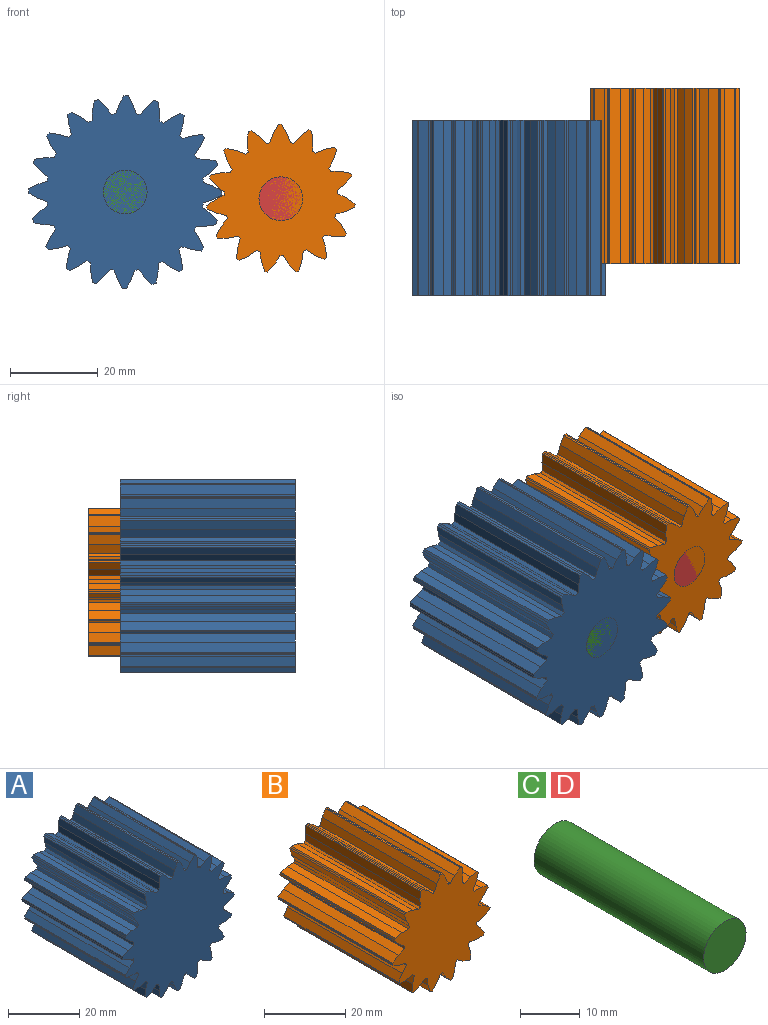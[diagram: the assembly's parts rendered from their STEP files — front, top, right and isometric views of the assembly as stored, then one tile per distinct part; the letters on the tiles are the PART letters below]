
ASSEMBLY  parts=4 mates=2
PART A: 142 faces, bbox 44x40x44 mm
  f0: plane 40x2.14mm, normal (-0.96,0,-0.28), area 89mm2, adj f1,f139,f140,f141
  f1: cylinder r=18mm len=40mm, axis (0,1,0), area 39.3mm2, adj f0,f2,f140,f141
  f2: plane 40x2.14mm, normal (0.28,0,0.96), area 89mm2, adj f1,f3,f140,f141
  f3: plane 40x2.29mm, normal (0.15,0,0.99), area 92.7mm2, adj f2,f4,f140,f141
  f4: plane 40x0.4mm, normal (-0.8,0,0.6), area 20mm2, adj f3,f5,f140,f141
  f5: plane 40x0.41mm, normal (-0.82,0,0.58), area 20mm2, adj f4,f6,f140,f141
  f6: plane 40x2.07mm, normal (-0.89,0,-0.45), area 92.7mm2, adj f5,f7,f140,f141
  f7: plane 40x1.84mm, normal (-0.83,0,-0.56), area 89mm2, adj f6,f8,f140,f141
  f8: cylinder r=18mm len=40mm, axis (0,1,0), area 39.3mm2, adj f7,f9,f140,f141
  f9: plane 40x2.22mm, normal (-0.03,0,1), area 89mm2, adj f8,f10,f140,f141
  f10: plane 40x2.29mm, normal (-0.16,0,0.99), area 92.7mm2, adj f9,f11,f140,f141
  f11: plane 40x0.47mm, normal (-0.95,0,0.32), area 20mm2, adj f10,f12,f140,f141
  f12: plane 40x0.48mm, normal (-0.95,0,0.3), area 20mm2, adj f11,f13,f140,f141
  f13: plane 40x1.65mm, normal (-0.71,0,-0.7), area 92.7mm2, adj f12,f14,f140,f141
  f14: plane 40x1.75mm, normal (-0.62,0,-0.79), area 89mm2, adj f13,f15,f140,f141
  f15: cylinder r=18mm len=40mm, axis (0,1,0), area 39.3mm2, adj f14,f16,f140,f141
  f16: plane 40x2.09mm, normal (-0.34,0,0.94), area 89mm2, adj f15,f17,f140,f141
  f17: plane 40x2.06mm, normal (-0.46,0,0.89), area 92.7mm2, adj f16,f18,f140,f141
  f18: plane 40x0.5mm, normal (-1,0,0.01), area 20mm2, adj f17,f19,f140,f141
  f19: plane 40x0.5mm, normal (-1,0,-0.01), area 20mm2, adj f18,f20,f140,f141
  f20: plane 40x2.06mm, normal (-0.46,0,-0.89), area 92.7mm2, adj f19,f21,f140,f141
  f21: plane 40x2.09mm, normal (-0.34,0,-0.94), area 89mm2, adj f20,f22,f140,f141
  f22: cylinder r=18mm len=40mm, axis (0,1,0), area 39.3mm2, adj f21,f23,f140,f141
  f23: plane 40x1.75mm, normal (-0.62,0,0.79), area 89mm2, adj f22,f24,f140,f141
  f24: plane 40x1.65mm, normal (-0.71,0,0.7), area 92.7mm2, adj f23,f25,f140,f141
  f25: plane 40x0.48mm, normal (-0.95,0,-0.3), area 20mm2, adj f24,f26,f140,f141
  f26: plane 40x0.47mm, normal (-0.95,0,-0.32), area 20mm2, adj f25,f27,f140,f141
  f27: plane 40x2.29mm, normal (-0.16,0,-0.99), area 92.7mm2, adj f26,f28,f140,f141
  f28: plane 40x2.22mm, normal (-0.03,0,-1), area 89mm2, adj f27,f29,f140,f141
  f29: cylinder r=18mm len=40mm, axis (0,1,0), area 39.3mm2, adj f28,f30,f140,f141
  f30: plane 40x1.84mm, normal (-0.83,0,0.56), area 89mm2, adj f29,f31,f140,f141
  f31: plane 40x2.07mm, normal (-0.89,0,0.45), area 92.7mm2, adj f30,f32,f140,f141
  f32: plane 40x0.41mm, normal (-0.82,0,-0.58), area 20mm2, adj f31,f33,f140,f141
  f33: plane 40x0.4mm, normal (-0.8,0,-0.6), area 20mm2, adj f32,f34,f140,f141
  f34: plane 40x2.29mm, normal (0.15,0,-0.99), area 92.7mm2, adj f33,f35,f140,f141
  f35: plane 40x2.14mm, normal (0.28,0,-0.96), area 89mm2, adj f34,f36,f140,f141
  f36: cylinder r=18mm len=40mm, axis (0,1,0), area 39.3mm2, adj f35,f37,f140,f141
  f37: plane 40x2.14mm, normal (-0.96,0,0.28), area 89mm2, adj f36,f38,f140,f141
  f38: plane 40x2.29mm, normal (-0.99,0,0.15), area 92.7mm2, adj f37,f39,f140,f141
  f39: plane 40x0.4mm, normal (-0.6,0,-0.8), area 20mm2, adj f38,f40,f140,f141
  f40: plane 40x0.41mm, normal (-0.58,0,-0.82), area 20mm2, adj f39,f41,f140,f141
  f41: plane 40x2.07mm, normal (0.45,0,-0.89), area 92.7mm2, adj f40,f42,f140,f141
  f42: plane 40x1.84mm, normal (0.56,0,-0.83), area 89mm2, adj f41,f43,f140,f141
  f43: cylinder r=18mm len=40mm, axis (0,1,0), area 39.3mm2, adj f42,f44,f140,f141
  f44: plane 40x2.22mm, normal (-1,0,-0.03), area 89mm2, adj f43,f45,f140,f141
  f45: plane 40x2.29mm, normal (-0.99,0,-0.16), area 92.7mm2, adj f44,f46,f140,f141
  f46: plane 40x0.47mm, normal (-0.32,0,-0.95), area 20mm2, adj f45,f47,f140,f141
  f47: plane 40x0.48mm, normal (-0.3,0,-0.95), area 20mm2, adj f46,f48,f140,f141
  f48: plane 40x1.65mm, normal (0.7,0,-0.71), area 92.7mm2, adj f47,f49,f140,f141
  f49: plane 40x1.75mm, normal (0.79,0,-0.62), area 89mm2, adj f48,f50,f140,f141
  f50: cylinder r=18mm len=40mm, axis (0,1,0), area 39.3mm2, adj f49,f51,f140,f141
  f51: plane 40x2.09mm, normal (-0.94,0,-0.34), area 89mm2, adj f50,f52,f140,f141
  f52: plane 40x2.06mm, normal (-0.89,0,-0.46), area 92.7mm2, adj f51,f53,f140,f141
  f53: plane 40x0.5mm, normal (-0.01,0,-1), area 20mm2, adj f52,f54,f140,f141
  f54: plane 40x0.5mm, normal (0.01,0,-1), area 20mm2, adj f53,f55,f140,f141
  f55: plane 40x2.06mm, normal (0.89,0,-0.46), area 92.7mm2, adj f54,f56,f140,f141
  f56: plane 40x2.09mm, normal (0.94,0,-0.34), area 89mm2, adj f55,f57,f140,f141
  f57: cylinder r=18mm len=40mm, axis (0,1,0), area 39.3mm2, adj f56,f58,f140,f141
  f58: plane 40x1.75mm, normal (-0.79,0,-0.62), area 89mm2, adj f57,f59,f140,f141
  f59: plane 40x1.65mm, normal (-0.7,0,-0.71), area 92.7mm2, adj f58,f60,f140,f141
  f60: plane 40x0.48mm, normal (0.3,0,-0.95), area 20mm2, adj f59,f61,f140,f141
  f61: plane 40x0.47mm, normal (0.32,0,-0.95), area 20mm2, adj f60,f62,f140,f141
  f62: plane 40x2.29mm, normal (0.99,0,-0.16), area 92.7mm2, adj f61,f63,f140,f141
  f63: plane 40x2.22mm, normal (1,0,-0.03), area 89mm2, adj f62,f64,f140,f141
  f64: cylinder r=18mm len=40mm, axis (0,1,0), area 39.3mm2, adj f63,f65,f140,f141
  f65: plane 40x1.84mm, normal (-0.56,0,-0.83), area 89mm2, adj f64,f66,f140,f141
  f66: plane 40x2.07mm, normal (-0.45,0,-0.89), area 92.7mm2, adj f65,f67,f140,f141
  f67: plane 40x0.41mm, normal (0.58,0,-0.82), area 20mm2, adj f66,f68,f140,f141
  f68: plane 40x0.4mm, normal (0.6,0,-0.8), area 20mm2, adj f67,f69,f140,f141
  f69: plane 40x2.29mm, normal (0.99,0,0.15), area 92.7mm2, adj f68,f70,f140,f141
  f70: plane 40x2.14mm, normal (0.96,0,0.28), area 89mm2, adj f69,f71,f140,f141
  f71: cylinder r=18mm len=40mm, axis (0,1,0), area 39.3mm2, adj f70,f72,f140,f141
  f72: plane 40x2.14mm, normal (-0.28,0,-0.96), area 89mm2, adj f71,f73,f140,f141
  f73: plane 40x2.29mm, normal (-0.15,0,-0.99), area 92.7mm2, adj f72,f74,f140,f141
  f74: plane 40x0.4mm, normal (0.8,0,-0.6), area 20mm2, adj f73,f75,f140,f141
  f75: plane 40x0.41mm, normal (0.82,0,-0.58), area 20mm2, adj f74,f76,f140,f141
  f76: plane 40x2.07mm, normal (0.89,0,0.45), area 92.7mm2, adj f75,f77,f140,f141
  f77: plane 40x1.84mm, normal (0.83,0,0.56), area 89mm2, adj f76,f78,f140,f141
  f78: cylinder r=18mm len=40mm, axis (0,1,0), area 39.3mm2, adj f77,f79,f140,f141
  f79: plane 40x2.22mm, normal (0.03,0,-1), area 89mm2, adj f78,f80,f140,f141
  f80: plane 40x2.29mm, normal (0.16,0,-0.99), area 92.7mm2, adj f79,f81,f140,f141
  f81: plane 40x0.47mm, normal (0.95,0,-0.32), area 20mm2, adj f80,f82,f140,f141
  f82: plane 40x0.48mm, normal (0.95,0,-0.3), area 20mm2, adj f81,f83,f140,f141
  f83: plane 40x1.65mm, normal (0.71,0,0.7), area 92.7mm2, adj f82,f84,f140,f141
  f84: plane 40x1.75mm, normal (0.62,0,0.79), area 89mm2, adj f83,f85,f140,f141
  f85: cylinder r=18mm len=40mm, axis (0,1,0), area 39.3mm2, adj f84,f86,f140,f141
  f86: plane 40x2.09mm, normal (0.34,0,-0.94), area 89mm2, adj f85,f87,f140,f141
  f87: plane 40x2.06mm, normal (0.46,0,-0.89), area 92.7mm2, adj f86,f88,f140,f141
  f88: plane 40x0.5mm, normal (1,0,-0.01), area 20mm2, adj f87,f89,f140,f141
  f89: plane 40x0.5mm, normal (1,0,0.01), area 20mm2, adj f88,f90,f140,f141
  f90: plane 40x2.06mm, normal (0.46,0,0.89), area 92.7mm2, adj f89,f91,f140,f141
  f91: plane 40x2.09mm, normal (0.34,0,0.94), area 89mm2, adj f90,f92,f140,f141
  f92: cylinder r=18mm len=40mm, axis (0,1,0), area 39.3mm2, adj f91,f93,f140,f141
  f93: plane 40x1.75mm, normal (0.62,0,-0.79), area 89mm2, adj f92,f94,f140,f141
  f94: plane 40x1.65mm, normal (0.71,0,-0.7), area 92.7mm2, adj f93,f95,f140,f141
  f95: plane 40x0.48mm, normal (0.95,0,0.3), area 20mm2, adj f94,f96,f140,f141
  f96: plane 40x0.47mm, normal (0.95,0,0.32), area 20mm2, adj f95,f97,f140,f141
  f97: plane 40x2.29mm, normal (0.16,0,0.99), area 92.7mm2, adj f96,f98,f140,f141
  f98: plane 40x2.22mm, normal (0.03,0,1), area 89mm2, adj f97,f99,f140,f141
  f99: cylinder r=18mm len=40mm, axis (0,1,0), area 39.3mm2, adj f98,f100,f140,f141
  f100: plane 40x1.84mm, normal (0.83,0,-0.56), area 89mm2, adj f99,f101,f140,f141
  f101: plane 40x2.07mm, normal (0.89,0,-0.45), area 92.7mm2, adj f100,f102,f140,f141
  f102: plane 40x0.41mm, normal (0.82,0,0.58), area 20mm2, adj f101,f103,f140,f141
  f103: plane 40x0.4mm, normal (0.8,0,0.6), area 20mm2, adj f102,f104,f140,f141
  f104: plane 40x2.29mm, normal (-0.15,0,0.99), area 92.7mm2, adj f103,f105,f140,f141
  f105: plane 40x2.14mm, normal (-0.28,0,0.96), area 89mm2, adj f104,f106,f140,f141
  f106: cylinder r=18mm len=40mm, axis (0,1,0), area 39.3mm2, adj f105,f107,f140,f141
  f107: plane 40x2.14mm, normal (0.96,0,-0.28), area 89mm2, adj f106,f108,f140,f141
  f108: plane 40x2.29mm, normal (0.99,0,-0.15), area 92.7mm2, adj f107,f109,f140,f141
  f109: plane 40x0.4mm, normal (0.6,0,0.8), area 20mm2, adj f108,f110,f140,f141
  f110: plane 40x0.41mm, normal (0.58,0,0.82), area 20mm2, adj f109,f111,f140,f141
  f111: plane 40x2.07mm, normal (-0.45,0,0.89), area 92.7mm2, adj f110,f112,f140,f141
  f112: plane 40x1.84mm, normal (-0.56,0,0.83), area 89mm2, adj f111,f113,f140,f141
  f113: cylinder r=18mm len=40mm, axis (0,1,0), area 39.3mm2, adj f112,f114,f140,f141
  f114: plane 40x2.22mm, normal (1,0,0.03), area 89mm2, adj f113,f115,f140,f141
  f115: plane 40x2.29mm, normal (0.99,0,0.16), area 92.7mm2, adj f114,f116,f140,f141
  f116: plane 40x0.47mm, normal (0.32,0,0.95), area 20mm2, adj f115,f117,f140,f141
  f117: plane 40x0.48mm, normal (0.3,0,0.95), area 20mm2, adj f116,f118,f140,f141
  f118: plane 40x1.65mm, normal (-0.7,0,0.71), area 92.7mm2, adj f117,f119,f140,f141
  f119: plane 40x1.75mm, normal (-0.79,0,0.62), area 89mm2, adj f118,f120,f140,f141
  f120: cylinder r=18mm len=40mm, axis (0,1,0), area 39.3mm2, adj f119,f121,f140,f141
  f121: plane 40x2.09mm, normal (0.94,0,0.34), area 89mm2, adj f120,f122,f140,f141
  f122: plane 40x2.06mm, normal (0.89,0,0.46), area 92.7mm2, adj f121,f123,f140,f141
  f123: plane 40x0.5mm, normal (0.01,0,1), area 20mm2, adj f122,f124,f140,f141
  f124: plane 40x0.5mm, normal (-0.01,0,1), area 20mm2, adj f123,f125,f140,f141
  f125: plane 40x2.06mm, normal (-0.89,0,0.46), area 92.7mm2, adj f124,f126,f140,f141
  f126: plane 40x2.09mm, normal (-0.94,0,0.34), area 89mm2, adj f125,f127,f140,f141
  f127: cylinder r=18mm len=40mm, axis (0,1,0), area 39.3mm2, adj f126,f128,f140,f141
  f128: plane 40x1.75mm, normal (0.79,0,0.62), area 89mm2, adj f127,f129,f140,f141
  f129: plane 40x1.65mm, normal (0.7,0,0.71), area 92.7mm2, adj f128,f130,f140,f141
  f130: plane 40x0.48mm, normal (-0.3,0,0.95), area 20mm2, adj f129,f131,f140,f141
  f131: plane 40x0.47mm, normal (-0.32,0,0.95), area 20mm2, adj f130,f132,f140,f141
  f132: plane 40x2.29mm, normal (-0.99,0,0.16), area 92.7mm2, adj f131,f133,f140,f141
  f133: plane 40x2.22mm, normal (-1,0,0.03), area 89mm2, adj f132,f134,f140,f141
  f134: cylinder r=18mm len=40mm, axis (0,1,0), area 39.3mm2, adj f133,f135,f140,f141
  f135: plane 40x1.84mm, normal (0.56,0,0.83), area 89mm2, adj f134,f136,f140,f141
  f136: plane 40x2.07mm, normal (0.45,0,0.89), area 92.7mm2, adj f135,f137,f140,f141
  f137: plane 40x0.41mm, normal (-0.58,0,0.82), area 20mm2, adj f136,f138,f140,f141
  f138: plane 40x0.4mm, normal (-0.6,0,0.8), area 20mm2, adj f137,f139,f140,f141
  f139: plane 40x2.29mm, normal (-0.99,0,-0.15), area 92.7mm2, adj f0,f138,f140,f141
  f140: plane 44x44mm, normal (0,-1,0), area 1256.5mm2, adj f0,f1,f2,f3,f4,f5,f6,f7
  f141: plane 44x44mm, normal (0,1,0), area 1256.5mm2, adj f0,f1,f2,f3,f4,f5,f6,f7
PART B: 107 faces, bbox 33.9x40x33.7 mm
  f0: cylinder r=13mm len=40mm, axis (0,1,0), area 29.3mm2, adj f1,f104,f105,f106
  f1: plane 40x2.1mm, normal (0.37,0,0.93), area 90.7mm2, adj f0,f2,f105,f106
  f2: plane 40x2.35mm, normal (0.21,0,0.98), area 96mm2, adj f1,f3,f105,f106
  f3: plane 40x0.27mm, normal (-0.74,0,0.68), area 14.7mm2, adj f2,f4,f105,f106
  f4: plane 40x0.28mm, normal (-0.75,0,0.66), area 14.7mm2, adj f3,f5,f105,f106
  f5: plane 40x2.28mm, normal (-0.95,0,-0.31), area 96mm2, adj f4,f6,f105,f106
  f6: plane 40x2mm, normal (-0.88,0,-0.47), area 90.7mm2, adj f5,f7,f105,f106
  f7: cylinder r=13mm len=40mm, axis (0,1,0), area 29.3mm2, adj f6,f8,f105,f106
  f8: plane 40x2.27mm, normal (-0.03,0,1), area 90.7mm2, adj f7,f9,f105,f106
  f9: plane 40x2.35mm, normal (-0.21,0,0.98), area 96mm2, adj f8,f10,f105,f106
  f10: plane 40x0.35mm, normal (-0.95,0,0.32), area 14.7mm2, adj f9,f11,f105,f106
  f11: plane 40x0.35mm, normal (-0.95,0,0.3), area 14.7mm2, adj f10,f12,f105,f106
  f12: plane 40x1.78mm, normal (-0.74,0,-0.67), area 96mm2, adj f11,f13,f105,f106
  f13: plane 40x1.79mm, normal (-0.62,0,-0.79), area 90.7mm2, adj f12,f14,f105,f106
  f14: cylinder r=13mm len=40mm, axis (0,1,0), area 29.3mm2, adj f13,f15,f105,f106
  f15: plane 40x2.04mm, normal (-0.44,0,0.9), area 90.7mm2, adj f14,f16,f105,f106
  f16: plane 40x1.94mm, normal (-0.59,0,0.81), area 96mm2, adj f15,f17,f105,f106
  f17: plane 40x0.37mm, normal (-1,0,-0.09), area 14.7mm2, adj f16,f18,f105,f106
  f18: plane 40x0.36mm, normal (-0.99,0,-0.12), area 14.7mm2, adj f17,f19,f105,f106
  f19: plane 40x2.19mm, normal (-0.41,0,-0.91), area 96mm2, adj f18,f20,f105,f106
  f20: plane 40x2.2mm, normal (-0.24,0,-0.97), area 90.7mm2, adj f19,f21,f105,f106
  f21: cylinder r=13mm len=40mm, axis (0,1,0), area 29.3mm2, adj f20,f22,f105,f106
  f22: plane 40x1.74mm, normal (-0.77,0,0.64), area 90.7mm2, adj f21,f23,f105,f106
  f23: plane 40x2.08mm, normal (-0.87,0,0.5), area 96mm2, adj f22,f24,f105,f106
  f24: plane 40x0.32mm, normal (-0.87,0,-0.49), area 14.7mm2, adj f23,f25,f105,f106
  f25: plane 40x0.32mm, normal (-0.86,0,-0.51), area 14.7mm2, adj f24,f26,f105,f106
  f26: plane 40x2.4mm, normal (0,0,-1), area 96mm2, adj f25,f27,f105,f106
  f27: plane 40x2.23mm, normal (0.17,0,-0.98), area 90.7mm2, adj f26,f28,f105,f106
  f28: cylinder r=13mm len=40mm, axis (0,1,0), area 29.3mm2, adj f27,f29,f105,f106
  f29: plane 40x2.18mm, normal (-0.96,0,0.28), area 90.7mm2, adj f28,f30,f105,f106
  f30: plane 40x2.39mm, normal (-0.99,0,0.1), area 96mm2, adj f29,f31,f105,f106
  f31: plane 40x0.29mm, normal (-0.6,0,-0.8), area 14.7mm2, adj f30,f32,f105,f106
  f32: plane 40x0.3mm, normal (-0.58,0,-0.82), area 14.7mm2, adj f31,f33,f105,f106
  f33: plane 40x2.19mm, normal (0.41,0,-0.91), area 96mm2, adj f32,f34,f105,f106
  f34: plane 40x1.88mm, normal (0.56,0,-0.83), area 90.7mm2, adj f33,f35,f105,f106
  f35: cylinder r=13mm len=40mm, axis (0,1,0), area 29.3mm2, adj f34,f36,f105,f106
  f36: plane 40x2.25mm, normal (-0.99,0,-0.14), area 90.7mm2, adj f35,f37,f105,f106
  f37: plane 40x2.28mm, normal (-0.95,0,-0.31), area 96mm2, adj f36,f38,f105,f106
  f38: plane 40x0.36mm, normal (-0.22,0,-0.98), area 14.7mm2, adj f37,f39,f105,f106
  f39: plane 40x0.36mm, normal (-0.2,0,-0.98), area 14.7mm2, adj f38,f40,f105,f106
  f40: plane 40x1.78mm, normal (0.74,0,-0.67), area 96mm2, adj f39,f41,f105,f106
  f41: plane 40x1.92mm, normal (0.85,0,-0.53), area 90.7mm2, adj f40,f42,f105,f106
  f42: cylinder r=13mm len=40mm, axis (0,1,0), area 29.3mm2, adj f41,f43,f105,f106
  f43: plane 40x1.92mm, normal (-0.85,0,-0.53), area 90.7mm2, adj f42,f44,f105,f106
  f44: plane 40x1.78mm, normal (-0.74,0,-0.67), area 96mm2, adj f43,f45,f105,f106
  f45: plane 40x0.36mm, normal (0.2,0,-0.98), area 14.7mm2, adj f44,f46,f105,f106
  f46: plane 40x0.36mm, normal (0.22,0,-0.98), area 14.7mm2, adj f45,f47,f105,f106
  f47: plane 40x2.28mm, normal (0.95,0,-0.31), area 96mm2, adj f46,f48,f105,f106
  f48: plane 40x2.25mm, normal (0.99,0,-0.14), area 90.7mm2, adj f47,f49,f105,f106
  f49: cylinder r=13mm len=40mm, axis (0,1,0), area 29.3mm2, adj f48,f50,f105,f106
  f50: plane 40x1.88mm, normal (-0.56,0,-0.83), area 90.7mm2, adj f49,f51,f105,f106
  f51: plane 40x2.19mm, normal (-0.41,0,-0.91), area 96mm2, adj f50,f52,f105,f106
  f52: plane 40x0.3mm, normal (0.58,0,-0.82), area 14.7mm2, adj f51,f53,f105,f106
  f53: plane 40x0.29mm, normal (0.6,0,-0.8), area 14.7mm2, adj f52,f54,f105,f106
  f54: plane 40x2.39mm, normal (0.99,0,0.1), area 96mm2, adj f53,f55,f105,f106
  f55: plane 40x2.18mm, normal (0.96,0,0.28), area 90.7mm2, adj f54,f56,f105,f106
  f56: cylinder r=13mm len=40mm, axis (0,1,0), area 29.3mm2, adj f55,f57,f105,f106
  f57: plane 40x2.23mm, normal (-0.17,0,-0.98), area 90.7mm2, adj f56,f58,f105,f106
  f58: plane 40x2.4mm, normal (0,0,-1), area 96mm2, adj f57,f59,f105,f106
  f59: plane 40x0.32mm, normal (0.86,0,-0.51), area 14.7mm2, adj f58,f60,f105,f106
  f60: plane 40x0.32mm, normal (0.87,0,-0.49), area 14.7mm2, adj f59,f61,f105,f106
  f61: plane 40x2.08mm, normal (0.87,0,0.5), area 96mm2, adj f60,f62,f105,f106
  f62: plane 40x1.74mm, normal (0.77,0,0.64), area 90.7mm2, adj f61,f63,f105,f106
  f63: cylinder r=13mm len=40mm, axis (0,1,0), area 29.3mm2, adj f62,f64,f105,f106
  f64: plane 40x2.2mm, normal (0.24,0,-0.97), area 90.7mm2, adj f63,f65,f105,f106
  f65: plane 40x2.19mm, normal (0.41,0,-0.91), area 96mm2, adj f64,f66,f105,f106
  f66: plane 40x0.36mm, normal (0.99,0,-0.12), area 14.7mm2, adj f65,f67,f105,f106
  f67: plane 40x0.37mm, normal (1,0,-0.09), area 14.7mm2, adj f66,f68,f105,f106
  f68: plane 40x1.94mm, normal (0.59,0,0.81), area 96mm2, adj f67,f69,f105,f106
  f69: plane 40x2.04mm, normal (0.44,0,0.9), area 90.7mm2, adj f68,f70,f105,f106
  f70: cylinder r=13mm len=40mm, axis (0,1,0), area 29.3mm2, adj f69,f71,f105,f106
  f71: plane 40x1.79mm, normal (0.62,0,-0.79), area 90.7mm2, adj f70,f72,f105,f106
  f72: plane 40x1.78mm, normal (0.74,0,-0.67), area 96mm2, adj f71,f73,f105,f106
  f73: plane 40x0.35mm, normal (0.95,0,0.3), area 14.7mm2, adj f72,f74,f105,f106
  f74: plane 40x0.35mm, normal (0.95,0,0.32), area 14.7mm2, adj f73,f75,f105,f106
  f75: plane 40x2.35mm, normal (0.21,0,0.98), area 96mm2, adj f74,f76,f105,f106
  f76: plane 40x2.27mm, normal (0.03,0,1), area 90.7mm2, adj f75,f77,f105,f106
  f77: cylinder r=13mm len=40mm, axis (0,1,0), area 29.3mm2, adj f76,f78,f105,f106
  f78: plane 40x2mm, normal (0.88,0,-0.47), area 90.7mm2, adj f77,f79,f105,f106
  f79: plane 40x2.28mm, normal (0.95,0,-0.31), area 96mm2, adj f78,f80,f105,f106
  f80: plane 40x0.28mm, normal (0.75,0,0.66), area 14.7mm2, adj f79,f81,f105,f106
  f81: plane 40x0.27mm, normal (0.74,0,0.68), area 14.7mm2, adj f80,f82,f105,f106
  f82: plane 40x2.35mm, normal (-0.21,0,0.98), area 96mm2, adj f81,f83,f105,f106
  f83: plane 40x2.1mm, normal (-0.37,0,0.93), area 90.7mm2, adj f82,f84,f105,f106
  f84: cylinder r=13mm len=40mm, axis (0,1,0), area 29.3mm2, adj f83,f85,f105,f106
  f85: plane 40x2.26mm, normal (1,0,-0.07), area 90.7mm2, adj f84,f86,f105,f106
  f86: plane 40x2.39mm, normal (0.99,0,0.11), area 96mm2, adj f85,f87,f105,f106
  f87: plane 40x0.33mm, normal (0.42,0,0.91), area 14.7mm2, adj f86,f88,f105,f106
  f88: plane 40x0.34mm, normal (0.4,0,0.92), area 14.7mm2, adj f87,f89,f105,f106
  f89: plane 40x1.94mm, normal (-0.59,0,0.81), area 96mm2, adj f88,f90,f105,f106
  f90: plane 40x1.63mm, normal (-0.72,0,0.69), area 90.7mm2, adj f89,f91,f105,f106
  f91: cylinder r=13mm len=40mm, axis (0,1,0), area 29.3mm2, adj f90,f92,f105,f106
  f92: plane 40x2.13mm, normal (0.94,0,0.34), area 90.7mm2, adj f91,f93,f105,f106
  f93: plane 40x2.08mm, normal (0.87,0,0.5), area 96mm2, adj f92,f94,f105,f106
  f94: plane 40x0.37mm, normal (0.01,0,1), area 14.7mm2, adj f93,f95,f105,f106
  f95: plane 40x0.37mm, normal (-0.01,0,1), area 14.7mm2, adj f94,f96,f105,f106
  f96: plane 40x2.08mm, normal (-0.87,0,0.5), area 96mm2, adj f95,f97,f105,f106
  f97: plane 40x2.13mm, normal (-0.94,0,0.34), area 90.7mm2, adj f96,f98,f105,f106
  f98: cylinder r=13mm len=40mm, axis (0,1,0), area 29.3mm2, adj f97,f99,f105,f106
  f99: plane 40x1.63mm, normal (0.72,0,0.69), area 90.7mm2, adj f98,f100,f105,f106
  f100: plane 40x1.94mm, normal (0.59,0,0.81), area 96mm2, adj f99,f101,f105,f106
  f101: plane 40x0.34mm, normal (-0.4,0,0.92), area 14.7mm2, adj f100,f102,f105,f106
  f102: plane 40x0.33mm, normal (-0.42,0,0.91), area 14.7mm2, adj f101,f103,f105,f106
  f103: plane 40x2.39mm, normal (-0.99,0,0.11), area 96mm2, adj f102,f104,f105,f106
  f104: plane 40x2.26mm, normal (-1,0,-0.07), area 90.7mm2, adj f0,f103,f105,f106
  f105: plane 33.88x33.7mm, normal (0,-1,0), area 706.3mm2, adj f0,f1,f2,f3,f4,f5,f6,f7
  f106: plane 33.88x33.7mm, normal (0,1,0), area 706.3mm2, adj f0,f1,f2,f3,f4,f5,f6,f7
PART C: 3 faces, bbox 10x40x10 mm
  f0: cylinder r=5mm len=40mm, axis (0,1,0), area 1256.6mm2, adj f1,f2
  f1: plane 10x10mm, normal (0,-1,0), area 78.5mm2, adj f0
  f2: plane 10x10mm, normal (0,1,0), area 78.5mm2, adj f0
PART D: same geometry as C
PLACE A rot(axis=(0,1,0),0.5deg) t=(-80.53,0.76,-14.42)mm
PLACE B rot(axis=(0,1,0),119.3deg) t=(-44.97,8.03,-15.97)mm
PLACE C t=(-112.51,0.76,-71.06)mm fixed
PLACE D t=(-76.95,8.03,-72.61)mm fixed
MATE revolute B.f7 <-> D.f0  axis (0,1,0) through (-44.97,8.03,-15.97)mm
MATE revolute A.f1 <-> C.f0  axis (0,1,0) through (-80.53,0.76,-14.42)mm
